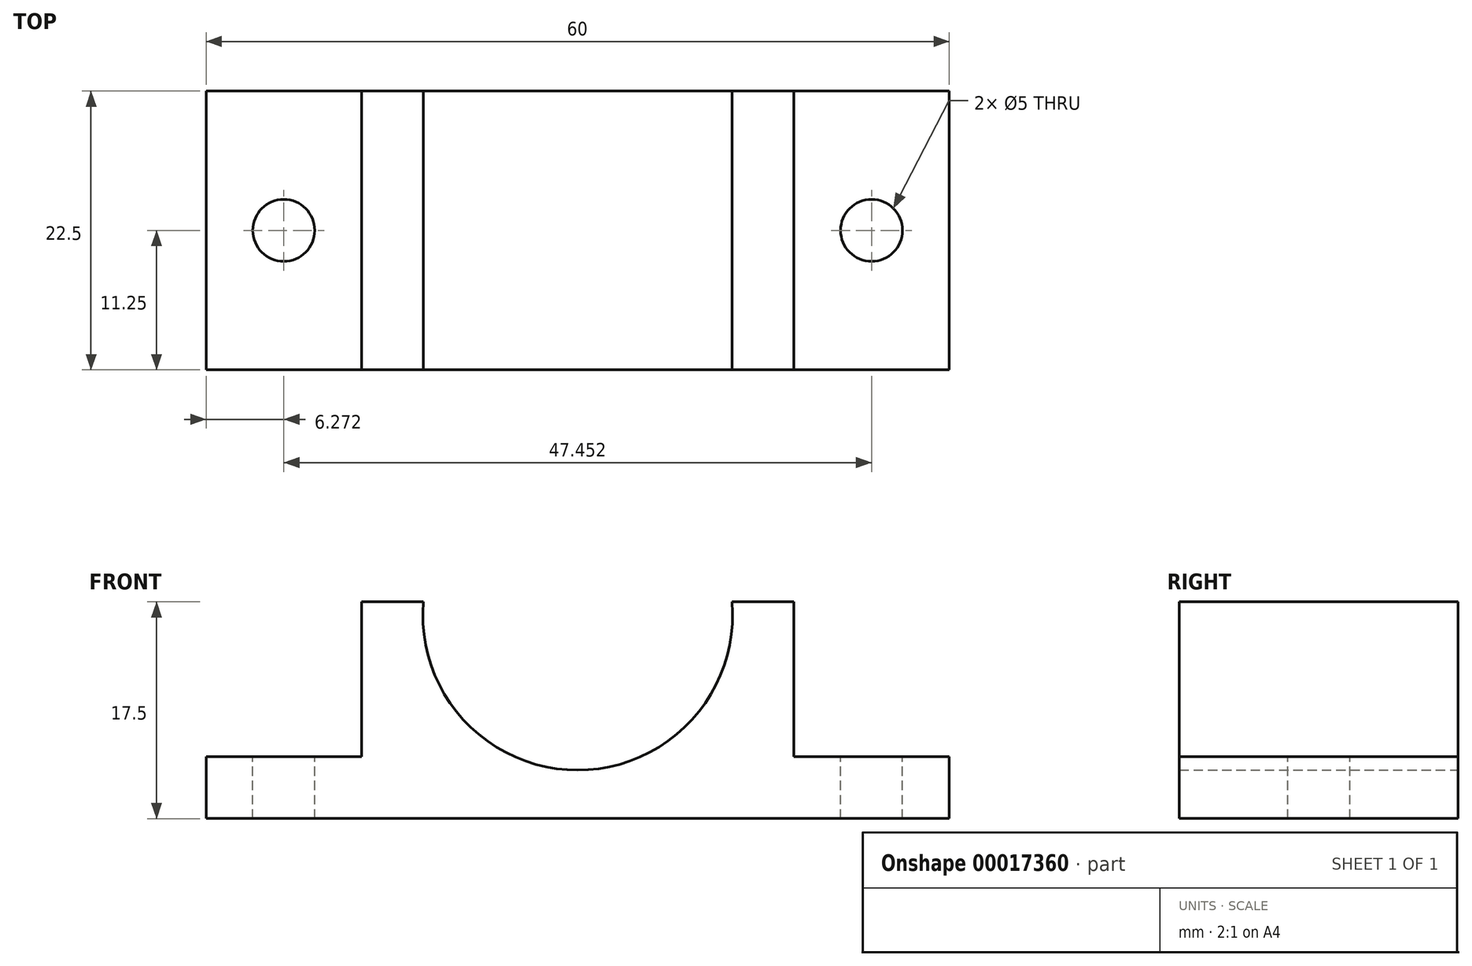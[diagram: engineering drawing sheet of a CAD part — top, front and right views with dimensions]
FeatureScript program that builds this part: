
annotation { "Feature Type Name" : "Feature", "Feature Type Description" : "" }
export const myFeature = defineFeature(function(context is Context, id is Id, definition is map)
    precondition{}
    {
        {
            var Q0;
            Q0=qCreatedBy(makeId("Front.planeOp"),FACE);
            var sketch = newSketch(context, id + "F0", { "sketchPlane" : qUnion([Q0])});
            skLineSegment(sketch, "E0", {"start": v(-24.46, -19.48) * mm, "end": v(35.54, -19.48) * mm});
            skLineSegment(sketch, "E1", {"start": v(35.54, -19.48) * mm, "end": v(35.54, -14.48) * mm});
            skLineSegment(sketch, "E2", {"start": v(35.54, -14.48) * mm, "end": v(23, -14.48) * mm});
            skLineSegment(sketch, "E3", {"start": v(23, -14.48) * mm, "end": v(23, -1.98) * mm});
            skLineSegment(sketch, "E4", {"start": v(-11.91, -1.98) * mm, "end": v(-11.91, -14.48) * mm});
            skLineSegment(sketch, "E5", {"start": v(-11.91, -14.48) * mm, "end": v(-24.46, -14.48) * mm});
            skLineSegment(sketch, "E6", {"start": v(-24.46, -19.48) * mm, "end": v(-24.46, -14.48) * mm});
            skLineSegment(sketch, "E7", {"start": v(-11.91, -1.98) * mm, "end": v(-6.91, -1.98) * mm});
            skLineSegment(sketch, "E8", {"start": v(23, -1.98) * mm, "end": v(18, -1.98) * mm});
            skArc(sketch, "E9", {"start": v(-6.91, -1.98) * mm, "mid": v(5.54, -15.57) * mm, "end": v(18, -1.98) * mm});
            skSolve(sketch);
        }
        {
            var Q0;
            Q0=makeQuery(id+"F0.imprint","IMPRINT",FACE,{"disambiguationData":[TD([[makeQuery(id+"F0.imprint","IMPRINT",EDGE,{"derivedFrom":sQuery(id+"F0.wireOp",EDGE,"E0")}),1.0]])]});
            extrude(context, id + "F1", {"entities" : qUnion([Q0]), "depth" : 22.5 * mm});
        }
        {
            var Q0;
            Q0=makeQuery(id+"F1.opExtrude","SWEPT_FACE",FACE,{"disambiguationData":[OSD([sQuery(id+"F0.wireOp",EDGE,"E2")])]});
            var sketch = newSketch(context, id + "F2", { "sketchPlane" : qUnion([Q0])});
            skCircle(sketch, "E10", {"center": v(29.26, -11.25) * mm, "radius": 2.5 * mm});
            skSolve(sketch);
        }
        {
            var Q0;
            Q0=makeQuery(id+"F1.opExtrude","SWEPT_FACE",FACE,{"disambiguationData":[OSD([sQuery(id+"F0.wireOp",EDGE,"E5")])]});
            var sketch = newSketch(context, id + "F3", { "sketchPlane" : qUnion([Q0])});
            skCircle(sketch, "E11", {"center": v(-18.19, -11.25) * mm, "radius": 2.5 * mm});
            skSolve(sketch);
        }
        {
            var Q0;
            Q0=makeQuery(id+"F2.imprint","IMPRINT",FACE,{"disambiguationData":[TD([[makeQuery(id+"F2.imprint","IMPRINT",EDGE,{"derivedFrom":sQuery(id+"F2.wireOp",EDGE,"E10")}),1.0]])]});
            extrude(context, id + "F4", {"entities" : qUnion([Q0]), "operationType" : NewBodyOperationType.REMOVE, "oppositeDirection" : true, "depth" : 25 * mm});
        }
        {
            var Q0;
            Q0=makeQuery(id+"F3.imprint","IMPRINT",FACE,{"disambiguationData":[TD([[makeQuery(id+"F3.imprint","IMPRINT",EDGE,{"derivedFrom":sQuery(id+"F3.wireOp",EDGE,"E11")}),1.0]])]});
            extrude(context, id + "F5", {"entities" : qUnion([Q0]), "operationType" : NewBodyOperationType.REMOVE, "oppositeDirection" : true, "depth" : 25 * mm});
        }
    });
